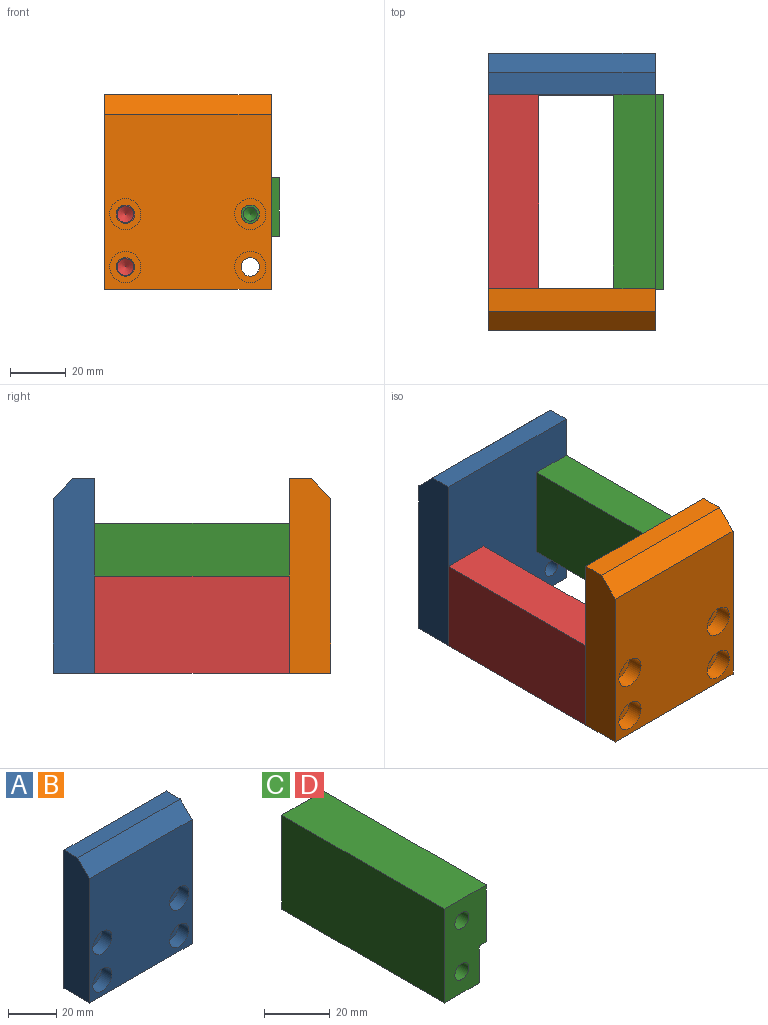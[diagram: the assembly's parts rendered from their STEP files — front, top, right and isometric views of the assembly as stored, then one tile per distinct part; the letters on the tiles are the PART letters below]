
ASSEMBLY  parts=4 mates=2
PART A: 19 faces, bbox 60x15x70 mm
  f0: plane 70x15mm, normal (-1,0,0), area 1025.5mm2, adj f1,f3,f4,f5,f6
  f1: plane 60x15mm, normal (0,0,-1), area 900mm2, adj f0,f2,f4,f5
  f2: plane 70x15mm, normal (1,0,0), area 1025.5mm2, adj f1,f3,f4,f5,f6
  f3: plane 60x8mm, normal (0,0,1), area 480mm2, adj f0,f2,f4,f6
  f4: plane 70x60mm, normal (0,1,0), area 4063.2mm2, adj f0,f1,f2,f3,f7,f10,f13,f16
  f5: plane 63x60mm, normal (0,-1,0), area 3382.4mm2, adj f0,f1,f2,f6,f9,f12,f15,f18
  f6: plane 60x7mm, normal (0,-0.71,0.71), area 594mm2, adj f0,f2,f3,f5
  f7: cylinder r=3.3mm len=9mm, axis (0,-1,0), area 186.6mm2, adj f4,f8
  f8: plane 11.25x11.25mm, normal (0,-1,0), area 65.2mm2, adj f7,f9
  f9: cylinder r=5.62mm len=11.25mm, axis (0,-1,0), area 212.1mm2, adj f5,f8
  f10: cylinder r=3.3mm len=9mm, axis (0,-1,0), area 186.6mm2, adj f4,f11
  f11: plane 11.25x11.25mm, normal (0,-1,0), area 65.2mm2, adj f10,f12
  f12: cylinder r=5.62mm len=11.25mm, axis (0,-1,0), area 212.1mm2, adj f5,f11
  f13: cylinder r=3.3mm len=9mm, axis (0,-1,0), area 186.6mm2, adj f4,f14
  f14: plane 11.25x11.25mm, normal (0,-1,0), area 65.2mm2, adj f13,f15
  f15: cylinder r=5.62mm len=11.25mm, axis (0,-1,0), area 212.1mm2, adj f5,f14
  f16: cylinder r=3.3mm len=9mm, axis (0,-1,0), area 186.6mm2, adj f4,f17
  f17: plane 11.25x11.25mm, normal (0,-1,0), area 65.2mm2, adj f16,f18
  f18: cylinder r=5.62mm len=11.25mm, axis (0,-1,0), area 212.1mm2, adj f5,f17
PART B: same geometry as A
PART C: 16 faces, bbox 18x70x35 mm
  f0: plane 70x35mm, normal (-1,0,0), area 2450mm2, adj f1,f5,f6,f7
  f1: plane 70x15mm, normal (0,0,-1), area 1050mm2, adj f0,f2,f6,f7
  f2: plane 70x13.77mm, normal (1,0,0), area 963.7mm2, adj f1,f3,f6,f7
  f3: plane 70x3mm, normal (0,0,-1), area 210mm2, adj f2,f4,f6,f7
  f4: plane 70x21.23mm, normal (1,0,0), area 1486.3mm2, adj f3,f5,f6,f7
  f5: plane 70x18mm, normal (0,0,1), area 1260mm2, adj f0,f4,f6,f7
  f6: plane 35x18mm, normal (0,1,0), area 549.4mm2, adj f0,f1,f2,f3,f4,f5,f13,f15
  f7: plane 35x18mm, normal (0,-1,0), area 532.1mm2, adj f0,f1,f2,f3,f4,f5,f9,f11
  f8: cone r=0mm half-angle=59deg, axis (0,-1,0), area 33mm2, adj f9
  f9: cylinder r=3mm len=12mm, axis (0,-1,0), area 226.2mm2, adj f7,f8
  f10: cone r=0mm half-angle=59deg, axis (0,-1,0), area 33mm2, adj f11
  f11: cylinder r=3mm len=12mm, axis (0,-1,0), area 226.2mm2, adj f7,f10
  f12: cone r=0mm half-angle=59deg, axis (0,1,0), area 22.9mm2, adj f13
  f13: cylinder r=2.5mm len=15mm, axis (0,1,0), area 235.6mm2, adj f6,f12
  f14: cone r=0mm half-angle=59deg, axis (0,1,0), area 22.9mm2, adj f15
  f15: cylinder r=2.5mm len=15mm, axis (0,1,0), area 235.6mm2, adj f6,f14
PART D: same geometry as C
PLACE A rot(axis=(0,0,1),180deg) t=(-71.51,28.96,-42.4)mm
PLACE B t=(-131.51,-71.04,-42.4)mm fixed
PLACE C rot(axis=(1,0,0),180deg) t=(-86.51,13.96,11.6)mm
PLACE D t=(-131.51,-56.04,-42.4)mm
MATE parallel C.f8 <-> A.f7  axis (0,1,0) through (-79.01,13.96,-15.4)mm
MATE cylindrical D.f8 <-> B.f7  axis (0,-1,0) through (-124.01,-56.04,-15.4)mm
